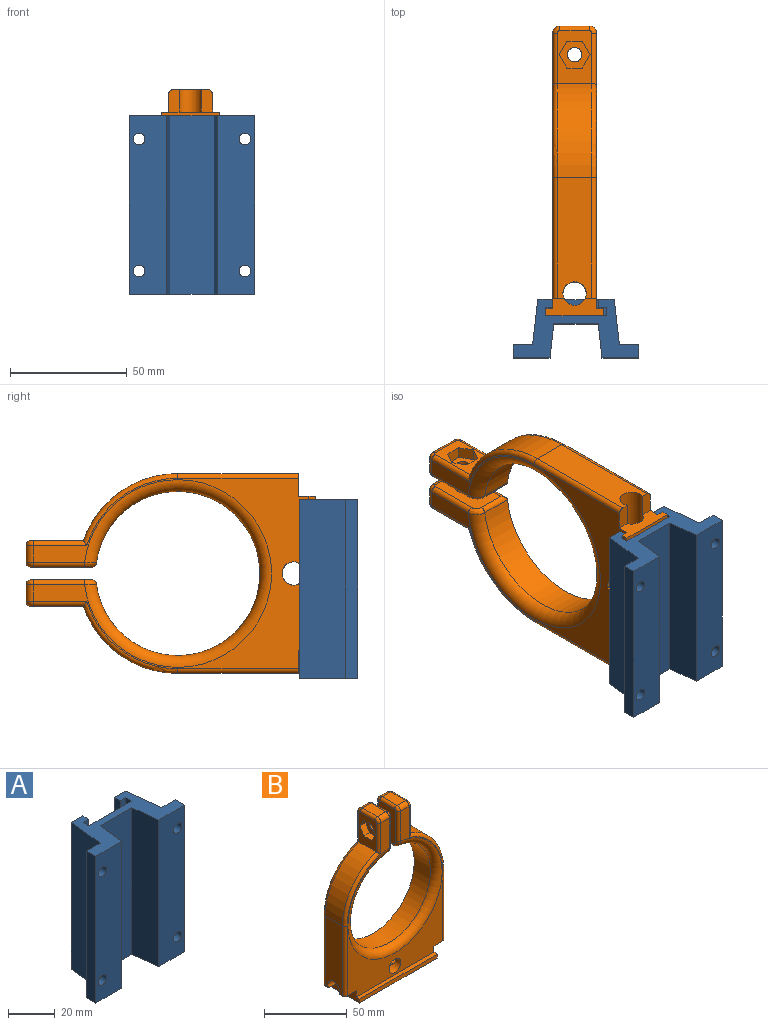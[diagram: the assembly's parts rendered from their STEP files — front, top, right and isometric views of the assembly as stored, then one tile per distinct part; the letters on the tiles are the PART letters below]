
ASSEMBLY  parts=2 mates=1
PART A: 26 faces, bbox 53.5x25x76.5 mm
  f0: plane 76.5x8.2mm, normal (0,1,0), area 588mm2, adj f5,f6,f7,f13,f24,f25
  f1: plane 76.5x8.2mm, normal (0,1,0), area 588mm2, adj f5,f11,f12,f13,f22,f23
  f2: plane 76.5x15.63mm, normal (0,-1,0), area 1156.8mm2, adj f5,f7,f8,f13,f24,f25
  f3: plane 76.5x15.63mm, normal (0,-1,0), area 1156.8mm2, adj f5,f10,f11,f13,f22,f23
  f4: plane 76.5x32.75mm, normal (0,1,0), area 1238.2mm2, adj f5,f6,f12,f13,f14,f20,f21
  f5: plane 53.51x25mm, normal (0,0,1), area 519mm2, adj f0,f1,f2,f3,f4,f6,f7,f8
  f6: plane 76.5x19.5mm, normal (-0.99,0.11,0), area 1501.1mm2, adj f0,f4,f5,f13
  f7: plane 76.5x5.5mm, normal (-1,0,0), area 420.8mm2, adj f0,f2,f5,f13
  f8: plane 76.5x14.5mm, normal (0.99,-0.11,0), area 1116.2mm2, adj f2,f5,f9,f13
  f9: plane 76.5x19mm, normal (0,-1,0), area 1453.5mm2, adj f5,f8,f10,f13
  f10: plane 76.5x14.5mm, normal (-0.99,-0.11,0), area 1116.2mm2, adj f3,f5,f9,f13
  f11: plane 76.5x5.5mm, normal (1,0,0), area 420.8mm2, adj f1,f3,f5,f13
  f12: plane 76.5x19.5mm, normal (0.99,0.11,0), area 1501.1mm2, adj f1,f4,f5,f13
  f13: plane 53.51x25mm, normal (0,0,-1), area 676.5mm2, adj f0,f1,f2,f3,f4,f6,f7,f8
  f14: plane 66x3.5mm, normal (1,0,0), area 231mm2, adj f4,f5,f15,f21
  f15: plane 66x3.3mm, normal (0,-1,0), area 217.8mm2, adj f5,f14,f16,f21
  f16: plane 66x3.5mm, normal (1,0,0), area 231mm2, adj f5,f15,f17,f21
  f17: plane 66x25.8mm, normal (0,1,0), area 1702.8mm2, adj f5,f16,f18,f21
  f18: plane 66x3.5mm, normal (-1,0,0), area 231mm2, adj f5,f17,f19,f21
  f19: plane 66x3.3mm, normal (0,-1,0), area 217.8mm2, adj f5,f18,f20,f21
  f20: plane 66x3.5mm, normal (-1,0,0), area 231mm2, adj f4,f5,f19,f21
  f21: plane 25.8x7mm, normal (0,0,1), area 157.5mm2, adj f4,f14,f15,f16,f17,f18,f19,f20
  f22: cylinder r=2.5mm len=5.5mm, axis (0,1,0), area 86.4mm2, adj f1,f3
  f23: cylinder r=2.5mm len=5.5mm, axis (0,1,0), area 86.4mm2, adj f1,f3
  f24: cylinder r=2.5mm len=5.5mm, axis (0,1,0), area 86.4mm2, adj f0,f2
  f25: cylinder r=2.5mm len=5.5mm, axis (0,1,0), area 86.4mm2, adj f0,f2
PART B: 81 faces, bbox 94.6x24.6x124 mm
  f0: plane 9.6x4.79mm, normal (0,0,-1), area 45.1mm2, adj f6,f12,f16,f43,f72
  f1: plane 9.6x4.79mm, normal (0,0,-1), area 45.1mm2, adj f8,f12,f24,f42,f63
  f2: cylinder r=5mm len=10mm, axis (0,-1,0), area 194.5mm2, adj f13,f42,f43
  f3: plane 22.5x14.75mm, normal (1,0,0), area 216.9mm2, adj f17,f32,f33,f34,f35,f36,f37,f76
  f4: plane 22.5x14.75mm, normal (-1,0,0), area 216.9mm2, adj f23,f25,f26,f27,f28,f29,f30,f67
  f5: plane 66.3x2.93mm, normal (0,0,1), area 193.9mm2, adj f6,f8,f9,f13
  f6: plane 24.6x7.44mm, normal (1,0,0), area 136.9mm2, adj f0,f5,f7,f9,f10,f11,f12,f13
  f7: plane 66.3x2.94mm, normal (0,1,0), area 194.9mm2, adj f6,f8,f10,f11
  f8: plane 24.6x7.44mm, normal (-1,0,0), area 136.9mm2, adj f1,f5,f7,f9,f10,f11,f12,f13
  f9: plane 66.3x2.94mm, normal (0,-1,0), area 194.9mm2, adj f5,f6,f8,f11
  f10: plane 66.3x2.93mm, normal (0,0,1), area 193.9mm2, adj f6,f7,f8,f12
  f11: plane 66.3x24.6mm, normal (0,0,-1), area 1631mm2, adj f6,f7,f8,f9
  f12: plane 118.04x81.5mm, normal (0,1,0), area 3422.9mm2, adj f0,f1,f6,f8,f10,f20,f41,f45
  f13: plane 118.04x81.5mm, normal (0,-1,0), area 2287.7mm2, adj f2,f5,f6,f8,f14,f15,f44,f47
  f14: plane 9.6x4.79mm, normal (0,0,-1), area 45.1mm2, adj f6,f13,f16,f43,f73
  f15: plane 9.6x4.79mm, normal (0,0,-1), area 45.1mm2, adj f8,f13,f24,f42,f64
  f16: plane 51.65x14.75mm, normal (1,0,0), area 703.1mm2, adj f0,f14,f17,f43,f72,f73
  f17: cylinder r=42.75mm len=40.39mm, axis (0,-1,0), area 780.1mm2, adj f3,f16,f74,f75
  f18: plane 12.75x7.25mm, normal (0,0,1), area 92.4mm2, adj f46,f48,f51,f80
  f19: plane 26.05x14.75mm, normal (-1,0,0), area 351.6mm2, adj f39,f49,f50,f51,f52,f53,f54,f55
  f20: cylinder r=35.15mm len=70.3mm, axis (0,-1,0), area 2912.8mm2, adj f12,f44,f54,f55,f61,f62
  f21: plane 26.05x14.75mm, normal (1,0,0), area 351.6mm2, adj f40,f56,f57,f58,f59,f60,f61,f62
  f22: plane 12.75x7.25mm, normal (0,0,1), area 92.4mm2, adj f45,f47,f58,f71
  f23: cylinder r=42.75mm len=40.39mm, axis (0,-1,0), area 780.1mm2, adj f4,f24,f65,f66
  f24: plane 51.65x14.75mm, normal (-1,0,0), area 703.1mm2, adj f1,f15,f23,f42,f63,f64
  f25: plane 5.75x5mm, normal (0,0.87,0.5), area 33.2mm2, adj f4,f26,f30,f31
  f26: plane 5.75x5mm, normal (0,0.87,-0.5), area 33.2mm2, adj f4,f25,f27,f31
  f27: plane 6.64x5mm, normal (0,0,-1), area 33.2mm2, adj f4,f26,f28,f31
  f28: plane 5.75x5mm, normal (0,-0.87,-0.5), area 33.2mm2, adj f4,f27,f29,f31
  f29: plane 5.75x5mm, normal (0,-0.87,0.5), area 33.2mm2, adj f4,f28,f30,f31
  f30: plane 6.64x5mm, normal (0,0,1), area 33.2mm2, adj f4,f25,f29,f31
  f31: plane 13.28x11.5mm, normal (-1,0,0), area 84.3mm2, adj f25,f26,f27,f28,f29,f30,f40
  f32: plane 6.64x5mm, normal (0,0,1), area 33.2mm2, adj f3,f33,f37,f38
  f33: plane 5.75x5mm, normal (0,-0.87,0.5), area 33.2mm2, adj f3,f32,f34,f38
  f34: plane 5.75x5mm, normal (0,-0.87,-0.5), area 33.2mm2, adj f3,f33,f35,f38
  f35: plane 6.64x5mm, normal (0,0,-1), area 33.2mm2, adj f3,f34,f36,f38
  f36: plane 5.75x5mm, normal (0,0.87,-0.5), area 33.2mm2, adj f3,f35,f37,f38
  f37: plane 5.75x5mm, normal (0,0.87,0.5), area 33.2mm2, adj f3,f32,f36,f38
  f38: plane 13.28x11.5mm, normal (1,0,0), area 84.3mm2, adj f32,f33,f34,f35,f36,f37,f39
  f39: cylinder r=3.1mm len=6.25mm, axis (-1,0,0), area 121.7mm2, adj f19,f38
  f40: cylinder r=3.1mm len=6.25mm, axis (-1,0,0), area 121.7mm2, adj f21,f31
  f41: cylinder r=5mm len=10mm, axis (0,-1,0), area 194.5mm2, adj f12,f42,f43
  f42: cylinder r=5mm len=42.75mm, axis (-1,0,0), area 1131.7mm2, adj f1,f2,f8,f15,f24,f41
  f43: cylinder r=5mm len=42.75mm, axis (-1,0,0), area 1131.7mm2, adj f0,f2,f6,f14,f16,f41
  f44: torus R=40.15mm, axis (0,-1,0), area 1752mm2, adj f13,f20,f52,f59
  f45: cylinder r=3mm len=7.25mm, axis (-1,0,0), area 34.2mm2, adj f12,f22,f60,f69
  f46: cylinder r=3mm len=7.25mm, axis (-1,0,0), area 34.2mm2, adj f12,f18,f53,f78
  f47: cylinder r=3mm len=7.25mm, axis (-1,0,0), area 34.2mm2, adj f13,f22,f56,f70
  f48: cylinder r=3mm len=7.25mm, axis (-1,0,0), area 34.2mm2, adj f13,f18,f49,f79
  f49: torus R=1mm, axis (1,0,0), area 11.2mm2, adj f19,f48,f50,f51
  f50: cylinder r=2mm len=22.02mm, axis (0,0,-1), area 69.2mm2, adj f13,f19,f49,f52
  f51: cylinder r=2mm len=12.75mm, axis (0,1,0), area 40.1mm2, adj f18,f19,f49,f53
  f52: bspline ~6.14x6.12mm, area 19.9mm2, adj f19,f44,f50,f54
  f53: torus R=1mm, axis (1,0,0), area 11.2mm2, adj f19,f46,f51,f55
  f54: cylinder r=2mm len=13.73mm, axis (0,-1,0), area 37.4mm2, adj f19,f20,f52,f55
  f55: cylinder r=2mm len=27.07mm, axis (0,0,-1), area 82.7mm2, adj f12,f19,f20,f53,f54
  f56: torus R=1mm, axis (1,0,0), area 11.2mm2, adj f21,f47,f57,f58
  f57: cylinder r=2mm len=22.02mm, axis (0,0,1), area 69.2mm2, adj f13,f21,f56,f59
  f58: cylinder r=2mm len=12.75mm, axis (0,-1,0), area 40.1mm2, adj f21,f22,f56,f60
  f59: bspline ~6.14x6.12mm, area 19.9mm2, adj f21,f44,f57,f61
  f60: torus R=1mm, axis (1,0,0), area 11.2mm2, adj f21,f45,f58,f62
  f61: cylinder r=2mm len=13.73mm, axis (0,-1,0), area 37.4mm2, adj f20,f21,f59,f62
  f62: cylinder r=2mm len=27.07mm, axis (0,0,1), area 82.7mm2, adj f12,f20,f21,f60,f61
  f63: cylinder r=2mm len=51.65mm, axis (0,0,-1), area 162.3mm2, adj f1,f12,f24,f65
  f64: cylinder r=2mm len=51.65mm, axis (0,0,-1), area 162.3mm2, adj f13,f15,f24,f66
  f65: torus R=40.75mm, axis (0,-1,0), area 164.9mm2, adj f12,f23,f63,f67
  f66: torus R=40.75mm, axis (0,-1,0), area 164.9mm2, adj f13,f23,f64,f68
  f67: cylinder r=2mm len=22.95mm, axis (0,0,-1), area 69.2mm2, adj f4,f12,f65,f69
  f68: cylinder r=2mm len=22.95mm, axis (0,0,-1), area 69.2mm2, adj f4,f13,f66,f70
  f69: torus R=1mm, axis (1,0,0), area 11.2mm2, adj f4,f45,f67,f71
  f70: torus R=1mm, axis (1,0,0), area 11.2mm2, adj f4,f47,f68,f71
  f71: cylinder r=2mm len=12.75mm, axis (0,1,0), area 40.1mm2, adj f4,f22,f69,f70
  f72: cylinder r=2mm len=51.65mm, axis (0,0,1), area 162.3mm2, adj f0,f12,f16,f74
  f73: cylinder r=2mm len=51.65mm, axis (0,0,1), area 162.3mm2, adj f13,f14,f16,f75
  f74: torus R=40.75mm, axis (0,-1,0), area 164.9mm2, adj f12,f17,f72,f76
  f75: torus R=40.75mm, axis (0,-1,0), area 164.9mm2, adj f13,f17,f73,f77
  f76: cylinder r=2mm len=22.95mm, axis (0,0,1), area 69.2mm2, adj f3,f12,f74,f78
  f77: cylinder r=2mm len=22.95mm, axis (0,0,1), area 69.2mm2, adj f3,f13,f75,f79
  f78: torus R=1mm, axis (1,0,0), area 11.2mm2, adj f3,f46,f76,f80
  f79: torus R=1mm, axis (1,0,0), area 11.2mm2, adj f3,f48,f77,f80
  f80: cylinder r=2mm len=12.75mm, axis (0,-1,0), area 40.1mm2, adj f3,f18,f78,f79
PLACE A t=(-26.76,25,0)mm
PLACE B rot(axis=(-0.58,-0.58,-0.58),120deg) t=(-27.36,18,44.88)mm
MATE slider B.f6 <-> A.f5  axis (0,0,1) through (-39.66,18,78.03)mm
